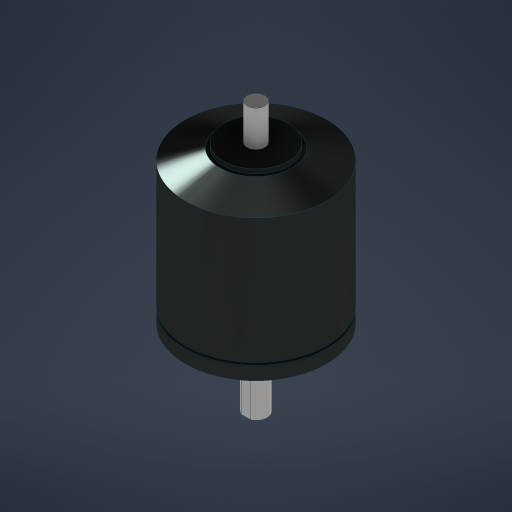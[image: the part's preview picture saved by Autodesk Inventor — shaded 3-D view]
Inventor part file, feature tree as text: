
AUTODESK INVENTOR PART (.ipt)
format: ipt  version: 2024 (Build 280153000, 153)  size: 269,312 bytes
history: native  units: in
note: dims shown in document units (in); Inventor stores cm internally (conversion verified against a paired STEP export)
features: thread x8, other x1
ambient origin geometry x8: Origin, YZ Plane, XZ Plane, XY Plane, X Axis, Y Axis, Z Axis, Center Point
bodies: Solid1 (feature_tree)
feature tree (9):
  thread  "Thread1"  [1 undecoded]
  thread  "Thread2"  [1 undecoded]
  thread  "Thread3"  [1 undecoded]
  thread  "Thread4"  [1 undecoded]
  thread  "Thread5"  [1 undecoded]
  thread  "Thread6"  [1 undecoded]
  thread  "Thread7"  [1 undecoded]
  thread  "Thread8"  [1 undecoded]
  other  "Part 1"
note: 8 required parameter values undecoded (feature->parameter linkage not recoverable at this tier; creation-order binding heuristic only, values carry confidence <= 0.55)
